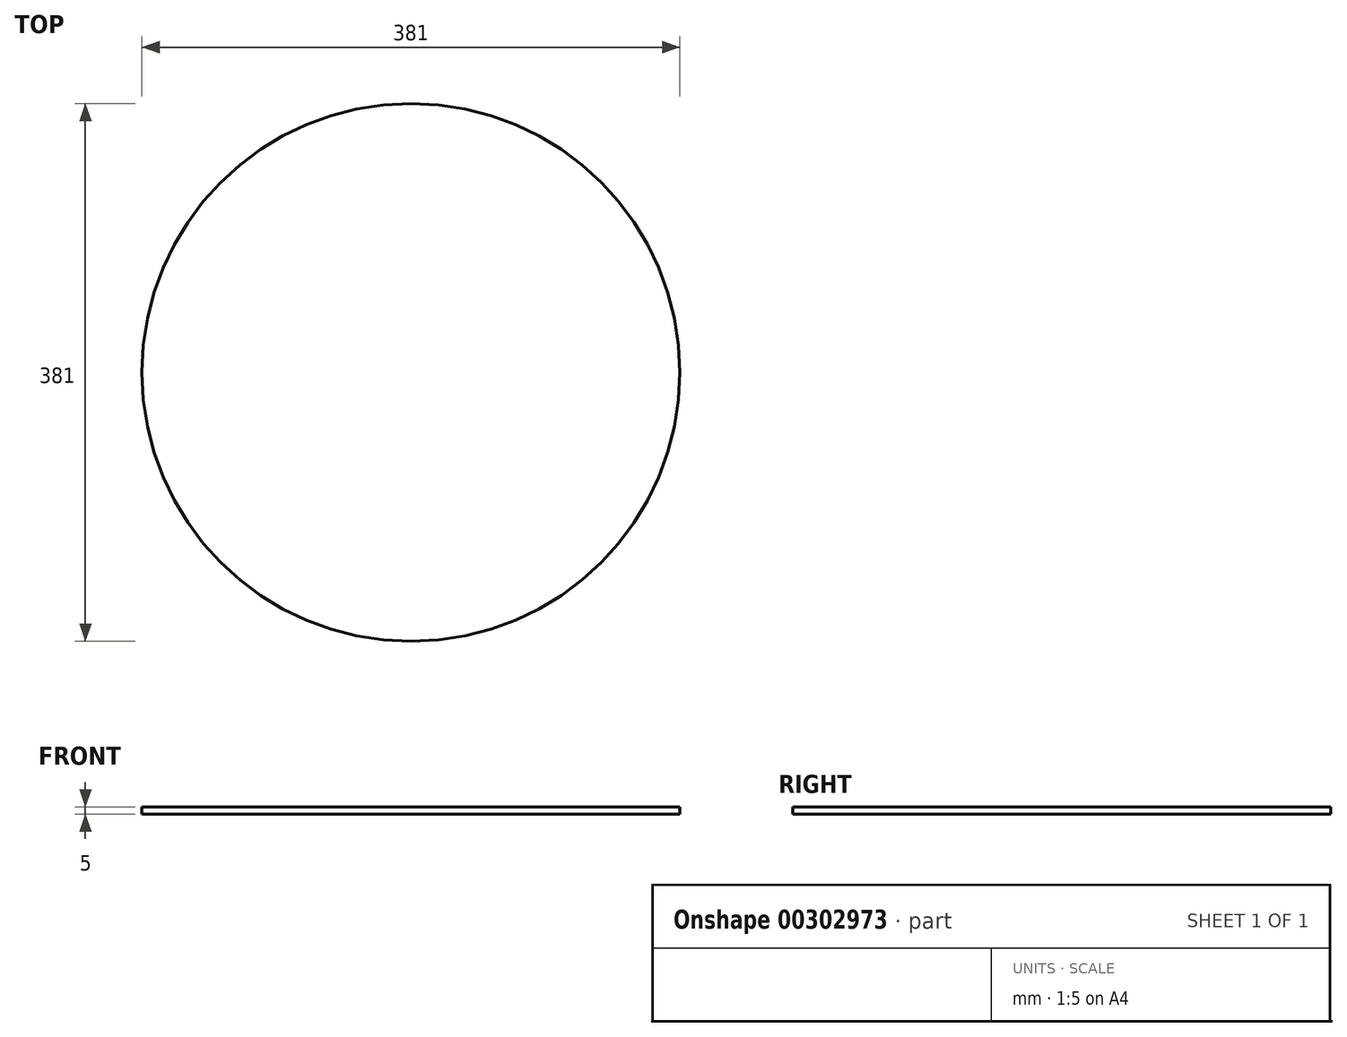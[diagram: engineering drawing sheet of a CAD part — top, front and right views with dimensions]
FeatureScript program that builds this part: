
annotation { "Feature Type Name" : "Feature", "Feature Type Description" : "" }
export const myFeature = defineFeature(function(context is Context, id is Id, definition is map)
    precondition{}
    {
        {
            var Q0;
            Q0=qCreatedBy(makeId("Top.planeOp"),FACE);
            var sketch = newSketch(context, id + "F0", { "sketchPlane" : qUnion([Q0])});
            skCircle(sketch, "E0", {"center": v(0, 0) * mm, "radius": 190.5 * mm});
            skSolve(sketch);
        }
        {
            var Q0;
            Q0=makeQuery(id+"F0.imprint","IMPRINT",FACE,{"disambiguationData":[TD([[makeQuery(id+"F0.imprint","IMPRINT",EDGE,{"derivedFrom":sQuery(id+"F0.wireOp",EDGE,"E0")}),1.0]])]});
            extrude(context, id + "F1", {"entities" : qUnion([Q0]), "depth" : 5 * mm});
        }
    });
